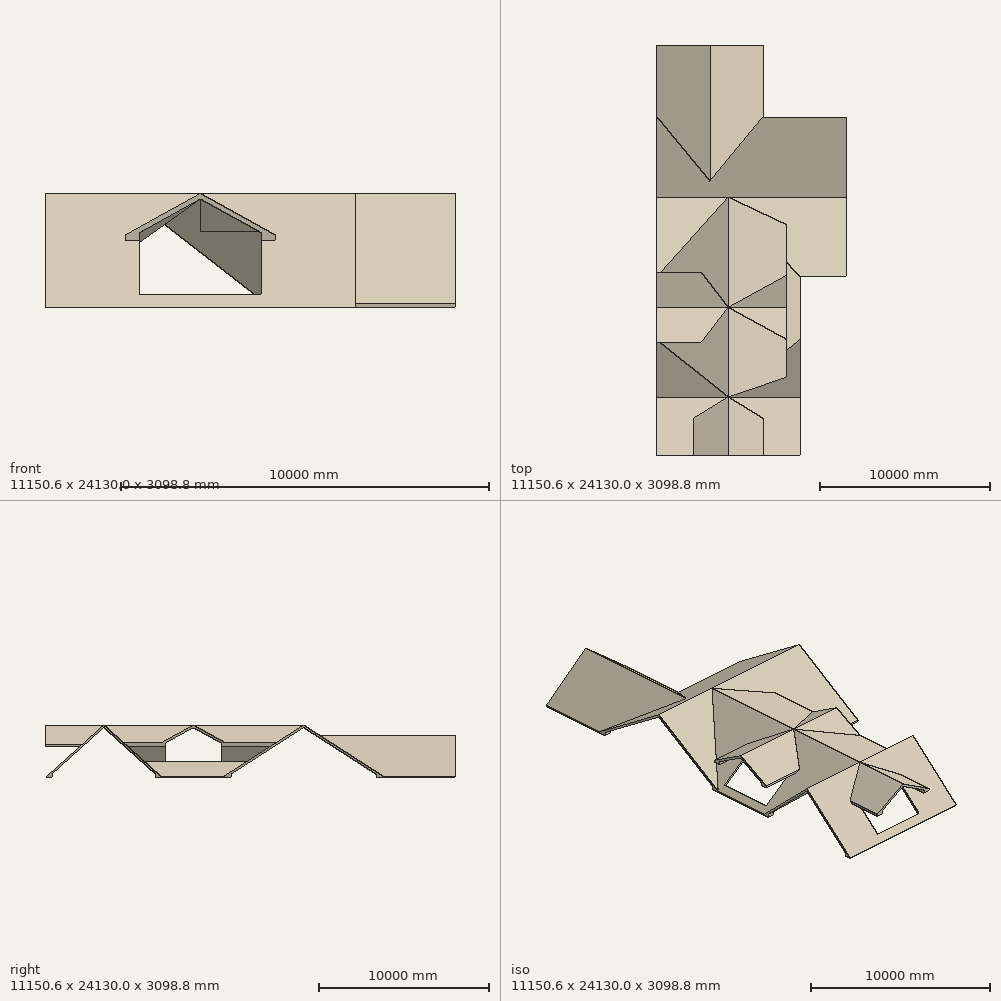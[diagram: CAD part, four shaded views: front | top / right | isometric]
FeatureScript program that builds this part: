
annotation { "Feature Type Name" : "Feature", "Feature Type Description" : "" }
export const myFeature = defineFeature(function(context is Context, id is Id, definition is map)
    precondition{}
    {
        {
            var Q0;
            Q0=qCreatedBy(makeId("Front.planeOp"),FACE);
            cPlane(context, id + "F0", {"entities" : qUnion([Q0]), "cplaneType" : CPlaneType.OFFSET, "offset" : 8928.1 * mm, "oppositeDirection" : true, "width" : 152.4 * mm, "height" : 152.4 * mm});
        }
        {
            var Q0;
            Q0=qCreatedBy(makeId("Front.planeOp"),FACE);
            cPlane(context, id + "F1", {"entities" : qUnion([Q0]), "cplaneType" : CPlaneType.OFFSET, "offset" : 6489.7 * mm, "width" : 152.4 * mm, "height" : 152.4 * mm});
        }
        {
            var Q0;
            Q0=qCreatedBy(makeId("Right.planeOp"),FACE);
            cPlane(context, id + "F2", {"entities" : qUnion([Q0]), "cplaneType" : CPlaneType.OFFSET, "offset" : 4216.4 * mm, "width" : 152.4 * mm, "height" : 152.4 * mm});
        }
        {
            var Q0;
            Q0=qCreatedBy(makeId("Front.planeOp"),FACE);
            cPlane(context, id + "F3", {"entities" : qUnion([Q0]), "cplaneType" : CPlaneType.OFFSET, "offset" : 11760.2 * mm, "width" : 152.4 * mm, "height" : 152.4 * mm});
        }
        {
            var Q0;
            Q0=qCreatedBy(makeId("Right.planeOp"),FACE);
            var sketch = newSketch(context, id + "F4", { "sketchPlane" : qUnion([Q0])});
            skLineSegment(sketch, "E0", {"start": v(-4267.2, 0) * mm, "end": v(4267.2, 0) * mm, "construction": true});
            skLineSegment(sketch, "E1", {"start": v(0, 0) * mm, "end": v(0, 2743.2) * mm, "construction": true});
            skLineSegment(sketch, "E2", {"start": v(0, 2743.2) * mm, "end": v(-4267.2, 0) * mm});
            skLineSegment(sketch, "E3", {"start": v(-4267.2, 0) * mm, "end": v(-4267.2, -203.2) * mm});
            skLineSegment(sketch, "E4", {"start": v(-4267.2, -203.2) * mm, "end": v(-4660.9, -203.2) * mm});
            skLineSegment(sketch, "E5", {"start": v(-4660.9, -203.2) * mm, "end": v(-4660.9, -100.7) * mm});
            skLineSegment(sketch, "E6", {"start": v(0, 2895.6) * mm, "end": v(-4660.9, -100.7) * mm});
            skLineSegment(sketch, "E7.MirrorCS", {"start": v(4267.2, 0) * mm, "end": v(4267.2, -203.2) * mm});
            skLineSegment(sketch, "E8.MirrorCS", {"start": v(4660.9, -203.2) * mm, "end": v(4660.9, -100.7) * mm});
            skLineSegment(sketch, "E9.MirrorCS", {"start": v(0, 2743.2) * mm, "end": v(4267.2, 0) * mm});
            skLineSegment(sketch, "E10.MirrorCS", {"start": v(4267.2, -203.2) * mm, "end": v(4660.9, -203.2) * mm});
            skLineSegment(sketch, "E11.MirrorCS", {"start": v(0, 2895.6) * mm, "end": v(4660.9, -100.7) * mm});
            skSolve(sketch);
        }
        {
            var Q0;
            Q0=qSketchRegion(id+"F4",true);
            extrude(context, id + "F5", {"entities" : qUnion([Q0]), "depth" : 11150.6 * mm});
        }
        {
            var Q0;
            Q0=qCreatedBy(id+"F0.planeOp",FACE);
            var sketch = newSketch(context, id + "F6", { "sketchPlane" : qUnion([Q0])});
            skLineSegment(sketch, "E12", {"start": v(393.7, 0) * mm, "end": v(5880.1, 0) * mm, "construction": true});
            skLineSegment(sketch, "E13", {"start": v(5880.1, 0) * mm, "end": v(5880.1, -203.2) * mm});
            skLineSegment(sketch, "E14", {"start": v(3136.9, 0) * mm, "end": v(3136.9, 2133.6) * mm, "construction": true});
            skLineSegment(sketch, "E15", {"start": v(5880.1, -203.2) * mm, "end": v(393.7, -203.2) * mm});
            skLineSegment(sketch, "E16", {"start": v(5880.1, 0) * mm, "end": v(3136.9, 2133.6) * mm});
            skLineSegment(sketch, "E17.MirrorCS", {"start": v(393.7, 0) * mm, "end": v(3136.9, 2133.6) * mm});
            skLineSegment(sketch, "E18.MirrorCS", {"start": v(393.7, 0) * mm, "end": v(393.7, -203.2) * mm});
            skSolve(sketch);
        }
        {
            var Q0;
            Q0=qSketchRegion(id+"F6",true);
            var Q1;
            Q1=qCreatedBy(makeId("Front.planeOp"),FACE);
            extrude(context, id + "F7", {"entities" : qUnion([Q0]), "operationType" : NewBodyOperationType.REMOVE, "endBound" : BoundingType.UP_TO_SURFACE, "endBoundEntityFace" : qUnion([Q1]), "depth" : 25.4 * mm});
        }
        {
            var Q0;
            Q0=qCreatedBy(id+"F0.planeOp",FACE);
            var sketch = newSketch(context, id + "F8", { "sketchPlane" : qUnion([Q0])});
            skLineSegment(sketch, "E19", {"start": v(393.7, 0) * mm, "end": v(5880.1, 0) * mm, "construction": true});
            skLineSegment(sketch, "E20", {"start": v(3136.9, 0) * mm, "end": v(3136.9, 2133.6) * mm, "construction": true});
            skLineSegment(sketch, "E21", {"start": v(5880.1, 0) * mm, "end": v(5880.1, -203.2) * mm});
            skLineSegment(sketch, "E22", {"start": v(5880.1, -203.2) * mm, "end": v(6273.8, -203.2) * mm});
            skLineSegment(sketch, "E23", {"start": v(6273.8, -203.2) * mm, "end": v(6273.8, -153.81) * mm});
            skLineSegment(sketch, "E24", {"start": v(5880.1, 0) * mm, "end": v(3136.9, 2133.6) * mm});
            skLineSegment(sketch, "E25", {"start": v(3136.9, 2286) * mm, "end": v(6273.8, -153.81) * mm});
            skLineSegment(sketch, "E26.MirrorCS", {"start": v(393.7, 0) * mm, "end": v(393.7, -203.2) * mm});
            skLineSegment(sketch, "E27.MirrorCS", {"start": v(0, -203.2) * mm, "end": v(0, -153.81) * mm});
            skLineSegment(sketch, "E28.MirrorCS", {"start": v(3136.9, 2286) * mm, "end": v(0, -153.81) * mm});
            skLineSegment(sketch, "E29.MirrorCS", {"start": v(393.7, -203.2) * mm, "end": v(0, -203.2) * mm});
            skLineSegment(sketch, "E30.MirrorCS", {"start": v(393.7, 0) * mm, "end": v(3136.9, 2133.6) * mm});
            skSolve(sketch);
        }
        {
            var Q0;
            Q0=qSketchRegion(id+"F8",true);
            extrude(context, id + "F9", {"entities" : qUnion([Q0]), "operationType" : NewBodyOperationType.ADD, "endBound" : BoundingType.UP_TO_NEXT, "depth" : 25.4 * mm});
        }
        {
            var Q0;
            Q0=qCreatedBy(makeId("Right.planeOp"),FACE);
            var sketch = newSketch(context, id + "F10", { "sketchPlane" : qUnion([Q0])});
            skLineSegment(sketch, "E31", {"start": v(-14808.2, 0) * mm, "end": v(-8712.2, 0) * mm, "construction": true});
            skLineSegment(sketch, "E32", {"start": v(-11760.2, 0) * mm, "end": v(-11760.2, 2743.2) * mm, "construction": true});
            skLineSegment(sketch, "E33", {"start": v(-11760.2, 2743.2) * mm, "end": v(-14808.2, 0) * mm});
            skLineSegment(sketch, "E34", {"start": v(-14808.2, -203.2) * mm, "end": v(-15201.9, -203.2) * mm});
            skLineSegment(sketch, "E35", {"start": v(-15201.9, -203.2) * mm, "end": v(-15201.9, -201.93) * mm});
            skLineSegment(sketch, "E36", {"start": v(-14808.2, 0) * mm, "end": v(-14808.2, -203.2) * mm});
            skLineSegment(sketch, "E37", {"start": v(-11760.2, 2895.6) * mm, "end": v(-15201.9, -201.93) * mm});
            skLineSegment(sketch, "E38.MirrorCS", {"start": v(-8318.5, -203.2) * mm, "end": v(-8318.5, -201.93) * mm});
            skLineSegment(sketch, "E39.MirrorCS", {"start": v(-8712.2, 0) * mm, "end": v(-8712.2, -203.2) * mm});
            skLineSegment(sketch, "E40.MirrorCS", {"start": v(-8712.2, -203.2) * mm, "end": v(-8318.5, -203.2) * mm});
            skLineSegment(sketch, "E41.MirrorCS", {"start": v(-11760.2, 2895.6) * mm, "end": v(-8318.5, -201.93) * mm});
            skLineSegment(sketch, "E42.MirrorCS", {"start": v(-11760.2, 2743.2) * mm, "end": v(-8712.2, 0) * mm});
            skSolve(sketch);
        }
        {
            var Q0;
            Q0=qSketchRegion(id+"F10",true);
            extrude(context, id + "F11", {"entities" : qUnion([Q0]), "operationType" : NewBodyOperationType.ADD, "depth" : 8432.8 * mm});
        }
        {
            var Q0;
            Q0=qCreatedBy(id+"F1.planeOp",FACE);
            var sketch = newSketch(context, id + "F12", { "sketchPlane" : qUnion([Q0])});
            skLineSegment(sketch, "E43", {"start": v(393.7, 0) * mm, "end": v(7226.3, 0) * mm, "construction": true});
            skLineSegment(sketch, "E44", {"start": v(4216.4, 0) * mm, "end": v(4216.4, 2743.2) * mm, "construction": true});
            skLineSegment(sketch, "E45", {"start": v(393.7, 0) * mm, "end": v(4216.4, 2743.2) * mm});
            skLineSegment(sketch, "E46", {"start": v(393.7, 0) * mm, "end": v(393.7, -203.2) * mm});
            skLineSegment(sketch, "E47", {"start": v(393.7, -203.2) * mm, "end": v(7226.3, -203.2) * mm});
            skLineSegment(sketch, "E48", {"start": v(7226.3, -203.2) * mm, "end": v(7226.3, 1828.8) * mm});
            skLineSegment(sketch, "E49", {"start": v(4216.4, 2743.2) * mm, "end": v(7226.3, 1828.8) * mm});
            skSolve(sketch);
        }
        {
            var Q0;
            Q0=qSketchRegion(id+"F12",true);
            var Q1;
            Q1=qCreatedBy(makeId("Front.planeOp"),FACE);
            var Q2;
            Q2=qCreatedBy(id+"F3.planeOp",FACE);
            extrude(context, id + "F13", {"entities" : qUnion([Q0]), "operationType" : NewBodyOperationType.REMOVE, "endBound" : BoundingType.UP_TO_SURFACE, "oppositeDirection" : true, "endBoundEntityFace" : qUnion([Q1]), "depth" : 25.4 * mm, "hasSecondDirection" : true, "secondDirectionBound" : SecondDirectionBoundingType.UP_TO_SURFACE, "secondDirectionOppositeDirection" : false, "secondDirectionBoundEntityFace" : qUnion([Q2]), "secondDirectionDepth" : 25.4 * mm});
        }
        {
            var Q0;
            Q0=qCreatedBy(id+"F1.planeOp",FACE);
            var sketch = newSketch(context, id + "F14", { "sketchPlane" : qUnion([Q0])});
            skLineSegment(sketch, "E50", {"start": v(393.7, 0) * mm, "end": v(8039.1, 0) * mm, "construction": true});
            skLineSegment(sketch, "E51", {"start": v(7226.3, 0) * mm, "end": v(7226.3, 1828.8) * mm, "construction": true});
            skLineSegment(sketch, "E52", {"start": v(4216.4, 0) * mm, "end": v(4216.4, 2743.2) * mm, "construction": true});
            skLineSegment(sketch, "E53", {"start": v(4216.4, 2743.2) * mm, "end": v(4216.4, 2895.6) * mm});
            skLineSegment(sketch, "E54", {"start": v(393.7, 0) * mm, "end": v(4216.4, 2743.2) * mm});
            skLineSegment(sketch, "E55", {"start": v(4216.4, 2895.6) * mm, "end": v(0, -130.12) * mm});
            skLineSegment(sketch, "E56", {"start": v(393.7, 0) * mm, "end": v(393.7, -203.2) * mm});
            skLineSegment(sketch, "E57", {"start": v(393.7, -203.2) * mm, "end": v(0, -203.2) * mm});
            skLineSegment(sketch, "E58", {"start": v(0, -203.2) * mm, "end": v(0, -130.12) * mm});
            skLineSegment(sketch, "E59.MirrorCS", {"start": v(8432.8, -203.2) * mm, "end": v(8432.8, -130.12) * mm});
            skLineSegment(sketch, "E60", {"start": v(8432.8, -203.2) * mm, "end": v(7226.3, -203.2) * mm});
            skLineSegment(sketch, "E61", {"start": v(7226.3, -203.2) * mm, "end": v(7226.3, 735.67) * mm});
            skLineSegment(sketch, "E62", {"start": v(7226.3, 735.67) * mm, "end": v(8432.8, -130.12) * mm});
            skLineSegment(sketch, "E63", {"start": v(4216.4, 2743.2) * mm, "end": v(7226.3, 1828.8) * mm});
            skLineSegment(sketch, "E64", {"start": v(7226.3, 1828.8) * mm, "end": v(7226.3, 1625.6) * mm});
            skLineSegment(sketch, "E65", {"start": v(7226.3, 1625.6) * mm, "end": v(7620, 1625.6) * mm});
            skLineSegment(sketch, "E66", {"start": v(7620, 1625.6) * mm, "end": v(7620, 1861.6) * mm});
            skLineSegment(sketch, "E67", {"start": v(4216.4, 2895.6) * mm, "end": v(7620, 1861.6) * mm});
            skSolve(sketch);
        }
        {
            var Q0;
            Q0=qSketchRegion(id+"F14",true);
            extrude(context, id + "F15", {"entities" : qUnion([Q0]), "operationType" : NewBodyOperationType.ADD, "endBound" : BoundingType.UP_TO_NEXT, "oppositeDirection" : true, "depth" : 25.4 * mm, "hasSecondDirection" : true, "secondDirectionBound" : SecondDirectionBoundingType.UP_TO_NEXT, "secondDirectionOppositeDirection" : false, "secondDirectionDepth" : 25.4 * mm});
        }
        {
            var Q0;
            Q0=makeQuery(id+"F15.opExtrude","SWEPT_FACE",FACE,{"disambiguationData":[OSD([sQuery(id+"F14.wireOp",EDGE,"E66")])]});
            var sketch = newSketch(context, id + "F16", { "sketchPlane" : qUnion([Q0])});
            skLineSegment(sketch, "E68", {"start": v(0, 0) * mm, "end": v(-6489.7, 0) * mm, "construction": true});
            skLineSegment(sketch, "E69", {"start": v(-6489.7, 0) * mm, "end": v(-6489.7, 2743.2) * mm, "construction": true});
            skLineSegment(sketch, "E70", {"start": v(-6489.7, 0) * mm, "end": v(-8140.7, 0) * mm, "construction": true});
            skLineSegment(sketch, "E71", {"start": v(-8140.7, 0) * mm, "end": v(-8140.7, 1828.8) * mm, "construction": true});
            skLineSegment(sketch, "E72", {"start": v(-6489.7, 2743.2) * mm, "end": v(-8140.7, 1828.8) * mm});
            skLineSegment(sketch, "E73", {"start": v(-8140.7, 1828.8) * mm, "end": v(-8140.7, 1625.6) * mm});
            skLineSegment(sketch, "E74", {"start": v(-8140.7, 1625.6) * mm, "end": v(-4838.7, 1625.6) * mm});
            skLineSegment(sketch, "E75.MirrorCS", {"start": v(-4838.7, 1828.8) * mm, "end": v(-4838.7, 1625.6) * mm});
            skLineSegment(sketch, "E76.MirrorCS", {"start": v(-6489.7, 2743.2) * mm, "end": v(-4838.7, 1828.8) * mm});
            skSolve(sketch);
        }
        {
            var Q0;
            Q0=qSketchRegion(id+"F16",true);
            var Q1;
            Q1=qCreatedBy(id+"F2.planeOp",FACE);
            extrude(context, id + "F17", {"entities" : qUnion([Q0]), "operationType" : NewBodyOperationType.REMOVE, "endBound" : BoundingType.UP_TO_SURFACE, "oppositeDirection" : true, "endBoundEntityFace" : qUnion([Q1]), "depth" : 25.4 * mm});
        }
        {
            var Q0;
            Q0=makeQuery(id+"F17.boolean.opBoolean","SPLIT",FACE,{"disambiguationData":[TD([makeQuery(id+"F5.opExtrude","SWEPT_FACE",FACE,{"disambiguationData":[OSD([sQuery(id+"F4.wireOp",EDGE,"E6")])]})])],"derivedFrom":makeQuery(id+"F15.opExtrude","SWEPT_FACE",FACE,{"disambiguationData":[OSD([sQuery(id+"F14.wireOp",EDGE,"E66")])]})});
            var sketch = newSketch(context, id + "F18", { "sketchPlane" : qUnion([Q0])});
            skLineSegment(sketch, "E77", {"start": v(0, 0) * mm, "end": v(-6489.7, 0) * mm, "construction": true});
            skLineSegment(sketch, "E78", {"start": v(-6489.7, 0) * mm, "end": v(-6489.7, 2743.2) * mm, "construction": true});
            skLineSegment(sketch, "E79", {"start": v(-6489.7, 0) * mm, "end": v(-8140.7, 0) * mm, "construction": true});
            skLineSegment(sketch, "E80", {"start": v(-8140.7, 0) * mm, "end": v(-8140.7, 1828.8) * mm, "construction": true});
            skLineSegment(sketch, "E81", {"start": v(-6489.7, 2743.2) * mm, "end": v(-8081.49, 1861.6) * mm});
            skLineSegment(sketch, "E82", {"start": v(-6489.7, 2895.6) * mm, "end": v(-8356.65, 1861.6) * mm});
            skLineSegment(sketch, "E83", {"start": v(-8356.65, 1861.6) * mm, "end": v(-8081.49, 1861.6) * mm});
            skLineSegment(sketch, "E84.MirrorCS", {"start": v(-4622.75, 1861.6) * mm, "end": v(-4897.91, 1861.6) * mm});
            skLineSegment(sketch, "E85.MirrorCS", {"start": v(-6489.7, 2895.6) * mm, "end": v(-4622.75, 1861.6) * mm});
            skLineSegment(sketch, "E86.MirrorCS", {"start": v(-6489.7, 2743.2) * mm, "end": v(-4897.91, 1861.6) * mm});
            skSolve(sketch);
        }
        {
            var Q0;
            Q0=qSketchRegion(id+"F18",true);
            var Q1;
            Q1=makeQuery(id+"F15.opExtrude","SWEPT_FACE",FACE,{"disambiguationData":[OSD([sQuery(id+"F14.wireOp",EDGE,"E67")])]});
            var Q2;
            Q2=qCreatedBy(id+"F2.planeOp",FACE);
            extrude(context, id + "F19", {"entities" : qUnion([Q0, Q1]), "operationType" : NewBodyOperationType.ADD, "endBound" : BoundingType.UP_TO_SURFACE, "oppositeDirection" : true, "endBoundEntityFace" : qUnion([Q2]), "depth" : 25.4 * mm});
        }
        {
            var Q0;
            {var subQ0=makeQuery(id+"F13.opExtrude","SWEPT_FACE",FACE,{"disambiguationData":[OSD([sQuery(id+"F12.wireOp",EDGE,"E46")])]});Q0=makeQuery(id+"F15.boolean.opBoolean","MERGE",FACE,{"derivedFrom":[makeQuery(id+"F13.boolean.opBoolean","COPY",FACE,{"disambiguationData":[OD(0.0)],"derivedFrom":subQ0}),makeQuery(id+"F13.boolean.opBoolean","COPY",FACE,{"disambiguationData":[OD(1.0)],"derivedFrom":subQ0}),makeQuery(id+"F15.opExtrude","SWEPT_FACE",FACE,{"disambiguationData":[OSD([sQuery(id+"F14.wireOp",EDGE,"E56")])]})]});}
            var sketch = newSketch(context, id + "F20", { "sketchPlane" : qUnion([Q0])});
            skLineSegment(sketch, "E87", {"start": v(0, 0) * mm, "end": v(-6489.7, 0) * mm, "construction": true});
            skLineSegment(sketch, "E88", {"start": v(-6489.7, 0) * mm, "end": v(-6489.7, 2743.2) * mm, "construction": true});
            skLineSegment(sketch, "E89", {"start": v(-8140.7, 0) * mm, "end": v(-4838.7, 0) * mm});
            skLineSegment(sketch, "E90", {"start": v(-8140.7, 0) * mm, "end": v(-8140.7, 1828.8) * mm});
            skLineSegment(sketch, "E91", {"start": v(-8140.7, 1828.8) * mm, "end": v(-6489.7, 2743.2) * mm});
            skLineSegment(sketch, "E92.MirrorCS", {"start": v(-4838.7, 0) * mm, "end": v(-4838.7, 1828.8) * mm});
            skLineSegment(sketch, "E93.MirrorCS", {"start": v(-4838.7, 1828.8) * mm, "end": v(-6489.7, 2743.2) * mm});
            skSolve(sketch);
        }
        {
            var Q0;
            Q0=qSketchRegion(id+"F20",true);
            var Q1;
            Q1=qCreatedBy(id+"F2.planeOp",FACE);
            extrude(context, id + "F21", {"entities" : qUnion([Q0]), "operationType" : NewBodyOperationType.REMOVE, "endBound" : BoundingType.UP_TO_SURFACE, "endBoundEntityFace" : qUnion([Q1]), "depth" : 25.4 * mm});
        }
        {
            var Q0;
            Q0=qCreatedBy(makeId("Right.planeOp"),FACE);
            var sketch = newSketch(context, id + "F22", { "sketchPlane" : qUnion([Q0])});
            skLineSegment(sketch, "E94", {"start": v(0, 0) * mm, "end": v(-6489.7, 0) * mm, "construction": true});
            skLineSegment(sketch, "E95", {"start": v(-8140.7, 0) * mm, "end": v(-6489.7, 0) * mm, "construction": true});
            skLineSegment(sketch, "E96", {"start": v(-6489.7, 0) * mm, "end": v(-6489.7, 2743.2) * mm, "construction": true});
            skLineSegment(sketch, "E97", {"start": v(-8140.7, 0) * mm, "end": v(-8140.7, 1828.8) * mm, "construction": true});
            skLineSegment(sketch, "E98", {"start": v(-6489.7, 2743.2) * mm, "end": v(-8140.7, 1828.8) * mm});
            skLineSegment(sketch, "E99", {"start": v(-8140.7, 1625.6) * mm, "end": v(-8534.4, 1625.6) * mm});
            skLineSegment(sketch, "E100", {"start": v(-8534.4, 1625.6) * mm, "end": v(-8534.4, 1763.15) * mm});
            skLineSegment(sketch, "E101", {"start": v(-8140.7, 1828.8) * mm, "end": v(-8140.7, 1625.6) * mm});
            skLineSegment(sketch, "E102", {"start": v(-6489.7, 2895.6) * mm, "end": v(-8534.4, 1763.15) * mm});
            skLineSegment(sketch, "E103.MirrorCS", {"start": v(-4838.7, 1828.8) * mm, "end": v(-4838.7, 1625.6) * mm});
            skLineSegment(sketch, "E104.MirrorCS", {"start": v(-4445, 1625.6) * mm, "end": v(-4445, 1763.15) * mm});
            skLineSegment(sketch, "E105.MirrorCS", {"start": v(-6489.7, 2895.6) * mm, "end": v(-4445, 1763.15) * mm});
            skLineSegment(sketch, "E106.MirrorCS", {"start": v(-4838.7, 1625.6) * mm, "end": v(-4445, 1625.6) * mm});
            skLineSegment(sketch, "E107.MirrorCS", {"start": v(-6489.7, 2743.2) * mm, "end": v(-4838.7, 1828.8) * mm});
            skSolve(sketch);
        }
        {
            var Q0;
            Q0=qSketchRegion(id+"F22",true);
            extrude(context, id + "F23", {"entities" : qUnion([Q0]), "operationType" : NewBodyOperationType.ADD, "endBound" : BoundingType.UP_TO_NEXT, "depth" : 25.4 * mm});
        }
        {
            var Q0;
            Q0=makeQuery(id+"F11.opExtrude","SWEPT_FACE",FACE,{"disambiguationData":[OSD([sQuery(id+"F10.wireOp",EDGE,"E36")])]});
            var sketch = newSketch(context, id + "F24", { "sketchPlane" : qUnion([Q0])});
            skLineSegment(sketch, "E108", {"start": v(-2565.4, 0) * mm, "end": v(-5867.4, 0) * mm});
            skLineSegment(sketch, "E109", {"start": v(-4216.4, 0) * mm, "end": v(-4216.4, 2743.2) * mm, "construction": true});
            skLineSegment(sketch, "E110", {"start": v(-2565.4, 0) * mm, "end": v(-2565.4, 1828.8) * mm});
            skLineSegment(sketch, "E111", {"start": v(-2565.4, 1828.8) * mm, "end": v(-4216.4, 2743.2) * mm});
            skLineSegment(sketch, "E112.MirrorCS", {"start": v(-5867.4, 1828.8) * mm, "end": v(-4216.4, 2743.2) * mm});
            skLineSegment(sketch, "E113.MirrorCS", {"start": v(-5867.4, 0) * mm, "end": v(-5867.4, 1828.8) * mm});
            skSolve(sketch);
        }
        {
            var Q0;
            Q0=qSketchRegion(id+"F24",true);
            var Q1;
            Q1=qCreatedBy(id+"F3.planeOp",FACE);
            extrude(context, id + "F25", {"entities" : qUnion([Q0]), "operationType" : NewBodyOperationType.REMOVE, "endBound" : BoundingType.UP_TO_SURFACE, "endBoundEntityFace" : qUnion([Q1]), "depth" : 25.4 * mm});
        }
        {
            var Q0;
            Q0=makeQuery(id+"F11.opExtrude","SWEPT_FACE",FACE,{"disambiguationData":[OSD([sQuery(id+"F10.wireOp",EDGE,"E35")])]});
            var sketch = newSketch(context, id + "F26", { "sketchPlane" : qUnion([Q0])});
            skLineSegment(sketch, "E114", {"start": v(2565.4, 0) * mm, "end": v(5867.4, 0) * mm, "construction": true});
            skLineSegment(sketch, "E115", {"start": v(4216.4, 0) * mm, "end": v(4216.4, 2743.2) * mm, "construction": true});
            skLineSegment(sketch, "E116", {"start": v(2565.4, 0) * mm, "end": v(2565.4, 1828.8) * mm, "construction": true});
            skLineSegment(sketch, "E117", {"start": v(4216.4, 2743.2) * mm, "end": v(2565.4, 1828.8) * mm});
            skLineSegment(sketch, "E118", {"start": v(2565.4, 1828.8) * mm, "end": v(2565.4, 1625.6) * mm});
            skLineSegment(sketch, "E119", {"start": v(2565.4, 1625.6) * mm, "end": v(2171.7, 1625.6) * mm});
            skLineSegment(sketch, "E120", {"start": v(2171.7, 1625.6) * mm, "end": v(2171.7, 1763.15) * mm});
            skLineSegment(sketch, "E121", {"start": v(4216.4, 2895.6) * mm, "end": v(2171.7, 1763.15) * mm});
            skLineSegment(sketch, "E122.MirrorCS", {"start": v(6261.1, 1625.6) * mm, "end": v(6261.1, 1763.15) * mm});
            skLineSegment(sketch, "E123.MirrorCS", {"start": v(4216.4, 2743.2) * mm, "end": v(5867.4, 1828.8) * mm});
            skLineSegment(sketch, "E124.MirrorCS", {"start": v(5867.4, 1828.8) * mm, "end": v(5867.4, 1625.6) * mm});
            skLineSegment(sketch, "E125.MirrorCS", {"start": v(5867.4, 1625.6) * mm, "end": v(6261.1, 1625.6) * mm});
            skLineSegment(sketch, "E126.MirrorCS", {"start": v(4216.4, 2895.6) * mm, "end": v(6261.1, 1763.15) * mm});
            skSolve(sketch);
        }
        {
            var Q0;
            Q0=qSketchRegion(id+"F26",true);
            extrude(context, id + "F27", {"entities" : qUnion([Q0]), "operationType" : NewBodyOperationType.ADD, "endBound" : BoundingType.UP_TO_NEXT, "oppositeDirection" : true, "depth" : 25.4 * mm});
        }
    });
